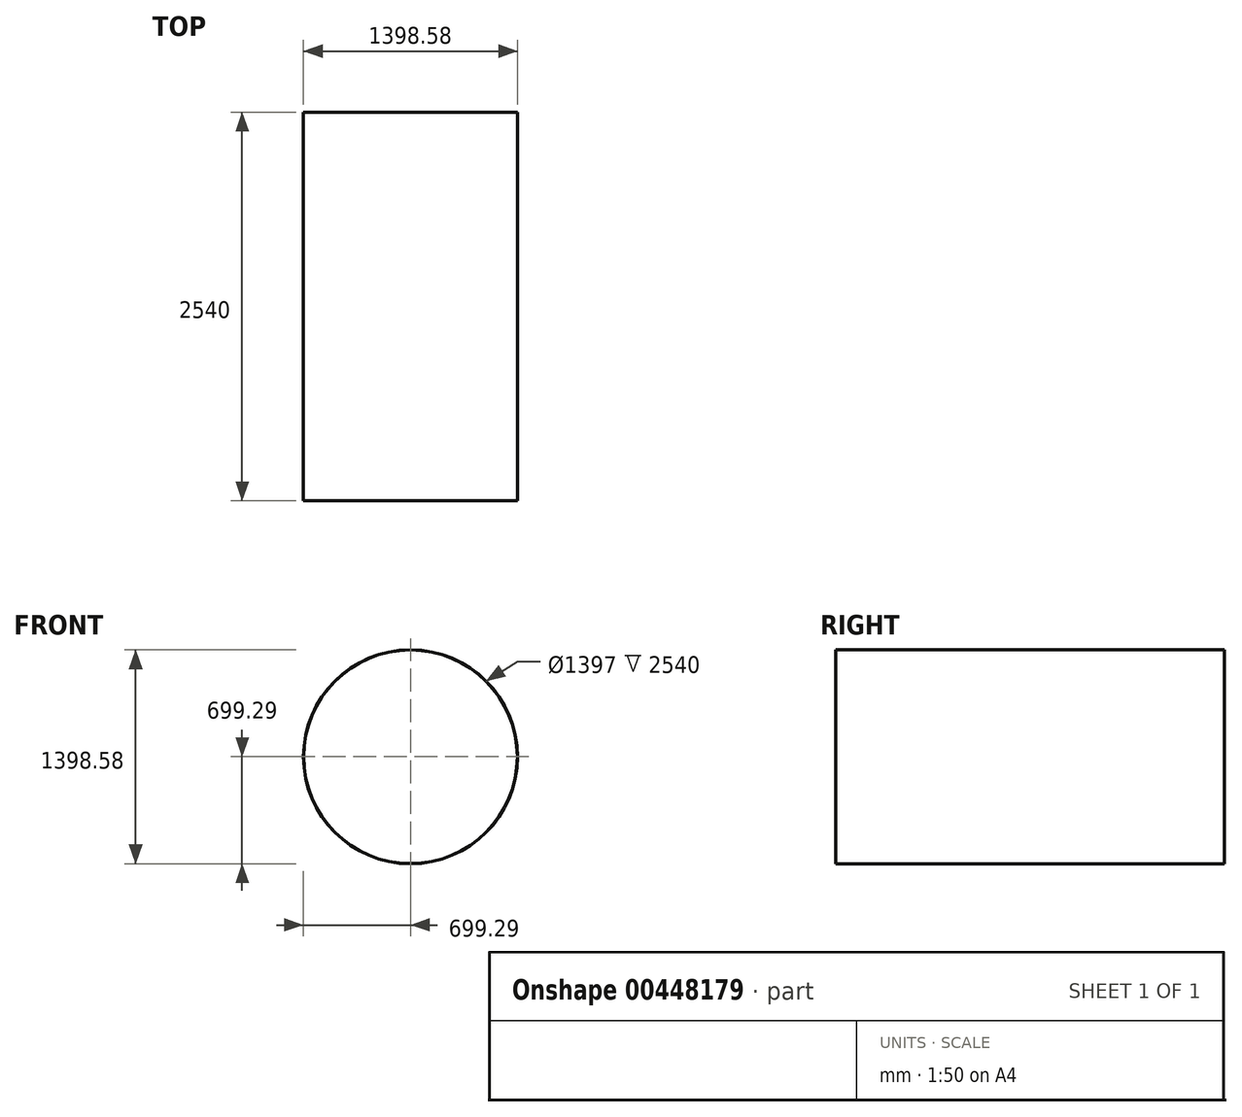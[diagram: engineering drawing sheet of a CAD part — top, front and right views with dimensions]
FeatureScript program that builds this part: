
annotation { "Feature Type Name" : "Feature", "Feature Type Description" : "" }
export const myFeature = defineFeature(function(context is Context, id is Id, definition is map)
    precondition{}
    {
        {
            var Q0;
            Q0=qCreatedBy(makeId("Front.planeOp"),FACE);
            var sketch = newSketch(context, id + "F0", { "sketchPlane" : qUnion([Q0])});
            skCircle(sketch, "E0", {"center": v(0, 0) * mm, "radius": 698.5 * mm});
            skCircle(sketch, "E1", {"center": v(0, 0) * mm, "radius": 699.3 * mm});
            skSolve(sketch);
        }
        {
            var Q0;
            Q0=makeQuery(id+"F0.imprint","IMPRINT",FACE,{"disambiguationData":[TD([[makeQuery(id+"F0.imprint","IMPRINT",EDGE,{"derivedFrom":sQuery(id+"F0.wireOp",EDGE,"E0")}),-1.0]])]});
            extrude(context, id + "F1", {"entities" : qUnion([Q0]), "oppositeDirection" : true, "depth" : 2540 * mm});
        }
    });
